# Revit family: ШТ-НСр 600х450
name_source: partatom
category: Обобщенные модели
units: mm (PartAtom-declared; Revit-internal decimal feet)

## family parameters
Может служить основой для арматурных стержней = Нет
Общий = Нет
Основа = Грань
При загрузке вырезать с полостями = Нет
Размер круглого соединителя = Использовать диаметр
Тип детали = Нормальный
Точка расчета площади = Нет

## types (15) — shared parameters
ADSK_URL документации изделия = https://www.ssd.ru
ADSK_URL страницы изделия = https://www.ssd.ru
ADSK_Единица измерения = шт
ADSK_Завод-изготовитель = АО СВЯЗЬСТРОЙДЕТАЛЬ
ADSK_Зона = -
ADSK_Количество = 1
ADSK_Материал обозначение = Серый RAL 7035
ADSK_Предел огнестойкости = -
ADSK_Размер_Глубина = 450 мм
ADSK_Размер_Ширина = 600 мм
Смещение двери = 426 мм

## per-type parameters (varying)
| type | ADSK_Код изделия | ADSK_Масса_Текст | ADSK_Наименование | ADSK_Размер_Высота | Высота двери | Дверь | Отметка по умолчанию |
| ШТ-НСр 6U (600х450мм) стеклянная дверь | 130411-00637 | 15,8 | Шкаф телекоммуникационный настенный разборный 19”,6U(600x450), ШТ-НСр-6U-600-450-С дверь стекло ССД | 360 мм | 280 мм | Дверь_С | 800 мм |
| ШТ-НСр 6U (600х450мм) металлическая дверь | 130411-00638 | 15,4 | Шкаф телекоммуникационный настенный разборный 19”,6U(600x450), ШТ-НСр-6U-600-450-М дверь металл ССД | 360 мм | 280 мм | Дверь_М | 800 мм |
| ШТ-НСр 6U (600х450мм) перфорированная дверь | 130411-00639 | 15,1 | Шкаф телекоммуникационный настенный разборный 19”,6U(600x450), ШТ-НСр-6U-600-450-П дверь перфорированная ССД | 360 мм | 280 мм | Дверь_П-6U | 800 мм |
| ШТ-НСр 9U (600х450мм) стеклянная дверь | 130411-00640 | 18,5 | Шкаф телекоммуникационный настенный разборный 19”,9U(600x450), ШТ-НСр-9U-600-450-С дверь стекло ССД | 493 мм | 413 мм | Дверь_С | 800 мм |
| ШТ-НСр 9U (600х450мм) металлическая дверь | 130411-00641 | 17,9 | Шкаф телекоммуникационный настенный разборный 19”,9U(600x450), ШТ-НСр-9U-600-450-М дверь металл ССД | 493 мм | 413 мм | Дверь_М | 800 мм |
| ШТ-НСр 9U (600х450мм) перфорированная дверь | 130411-00642 | 17,6 | Шкаф телекоммуникационный настенный разборный 19”,9U(600x450), ШТ-НСр-9U-600-450-П дверь перфорированная ССД | 493 мм | 413 мм | Дверь_П-9U | 800 мм |
| ШТ-НСр 12U (600х450мм) стеклянная дверь | 130411-00643 | 21,5 | Шкаф телекоммуникационный настенный разборный 19”,12U(600x450), ШТ-НСр-12U-600-450-С дверь стекло ССД | 626 мм | 546 мм | Дверь_С | 0 мм |
| ШТ-НСр 12U (600х450мм) металлическая двер | 130411-00644 | 20,4 | Шкаф телекоммуникационный настенный разборный 19”,12U(600x450), ШТ-НСр-12U-600-450-М дверь металл ССД | 626 мм | 546 мм | Дверь_М | 800 мм |
| ШТ-НСр 12U (600х450мм) перфорированная дверь | 130411-00645 | 20,1 | Шкаф телекоммуникационный настенный разборный 19”,12U(600x450), ШТ-НСр-12U-600-450-П дверь перфорированная ССД | 626 мм | 546 мм | Дверь_П-12U | 800 мм |
| ШТ-НСр 15U (600х450мм) стеклянная дверь | 130411-00646 | 23,8 | Шкаф телекоммуникационный настенный разборный 19”,15U(600x450), ШТ-НСр-15U-600-450-С дверь стекло ССД | 760 мм | 680 мм | Дверь_С | 800 мм |
| ШТ-НСр 15U (600х450мм) металлическая дверь | 130411-00647 | 22,9 | Шкаф телекоммуникационный настенный разборный 19”,15U(600x450), ШТ-НСр-15U-600-450-М дверь металл ССД | 760 мм | 680 мм | Дверь_М | 800 мм |
| ШТ-НСр 15U (600х450мм) перфорированная дверь | 130411-00648 | 22,5 | Шкаф телекоммуникационный настенный разборный 19”,15U(600x450), ШТ-НСр-15U-600-450-П дверь перфорированная ССД | 760 мм | 680 мм | Дверь_П-15U | 800 мм |
| ШТ-НСр 18U (600х450мм) стеклянная дверь | 130411-00649 | 26,5 | Шкаф телекоммуникационный настенный разборный 19”,18U(600x450), ШТ-НСр-18U-600-450-С дверь стекло ССД | 893 мм | 813 мм | Дверь_С | 800 мм |
| ШТ-НСр 18U (600х450мм) металлическая дверь | 130411-00650 | 25,4 | Шкаф телекоммуникационный настенный разборный 19”,18U(600x450), ШТ-НСр-18U-600-450-М дверь металл ССД | 893 мм | 813 мм | Дверь_М | 800 мм |
| ШТ-НСр 18U (600х450мм) перфорированная дверь | 130411-00651 | 25,0 | Шкаф телекоммуникационный настенный разборный 19”,18U(600x450), ШТ-НСр-18U-600-450-П дверь перфорированная ССД | 893 мм | 813 мм | Дверь_П-18U | 800 мм |

note: column(s) folded — value = type name in every type: ADSK_Обозначение
